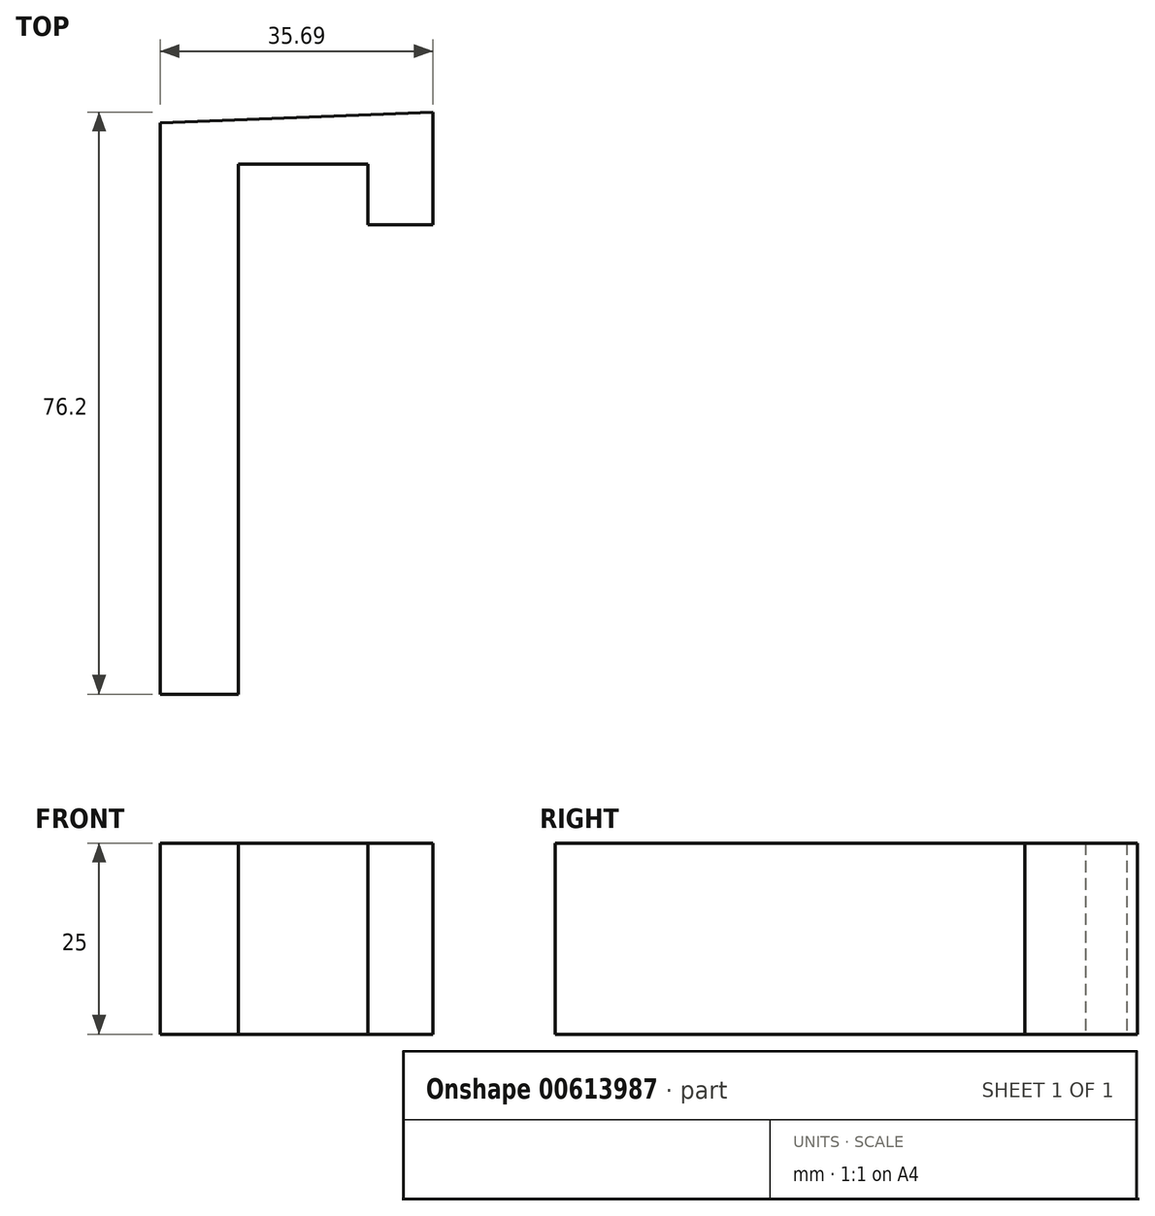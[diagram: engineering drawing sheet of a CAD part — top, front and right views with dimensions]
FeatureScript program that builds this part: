
annotation { "Feature Type Name" : "Feature", "Feature Type Description" : "" }
export const myFeature = defineFeature(function(context is Context, id is Id, definition is map)
    precondition{}
    {
        {
            var Q0;
            Q0=qCreatedBy(makeId("Top.planeOp"),FACE);
            var sketch = newSketch(context, id + "F0", { "sketchPlane" : qUnion([Q0])});
            skLineSegment(sketch, "E0", {"start": v(-53.68, 29.6) * mm, "end": v(-53.68, -45.18) * mm});
            skLineSegment(sketch, "E1", {"start": v(-53.68, -45.18) * mm, "end": v(-43.48, -45.18) * mm});
            skLineSegment(sketch, "E2", {"start": v(-43.48, -45.18) * mm, "end": v(-43.48, 24.22) * mm});
            skLineSegment(sketch, "E3", {"start": v(-43.48, 24.22) * mm, "end": v(-26.49, 24.22) * mm});
            skLineSegment(sketch, "E4", {"start": v(-26.49, 24.22) * mm, "end": v(-26.49, 16.29) * mm});
            skLineSegment(sketch, "E5", {"start": v(-26.49, 16.29) * mm, "end": v(-17.99, 16.29) * mm});
            skLineSegment(sketch, "E6", {"start": v(-17.99, 16.29) * mm, "end": v(-17.99, 31.02) * mm});
            skLineSegment(sketch, "E7", {"start": v(-17.99, 31.02) * mm, "end": v(-53.68, 29.6) * mm});
            skSolve(sketch);
        }
        {
            var Q0;
            Q0 = qSketchRegion(id + "F0", true);
            extrude(context, id + "F1", {"entities" : qUnion([Q0]), "depth" : 25 * mm, "offsetDistance" : 25 * mm});
        }
    });
